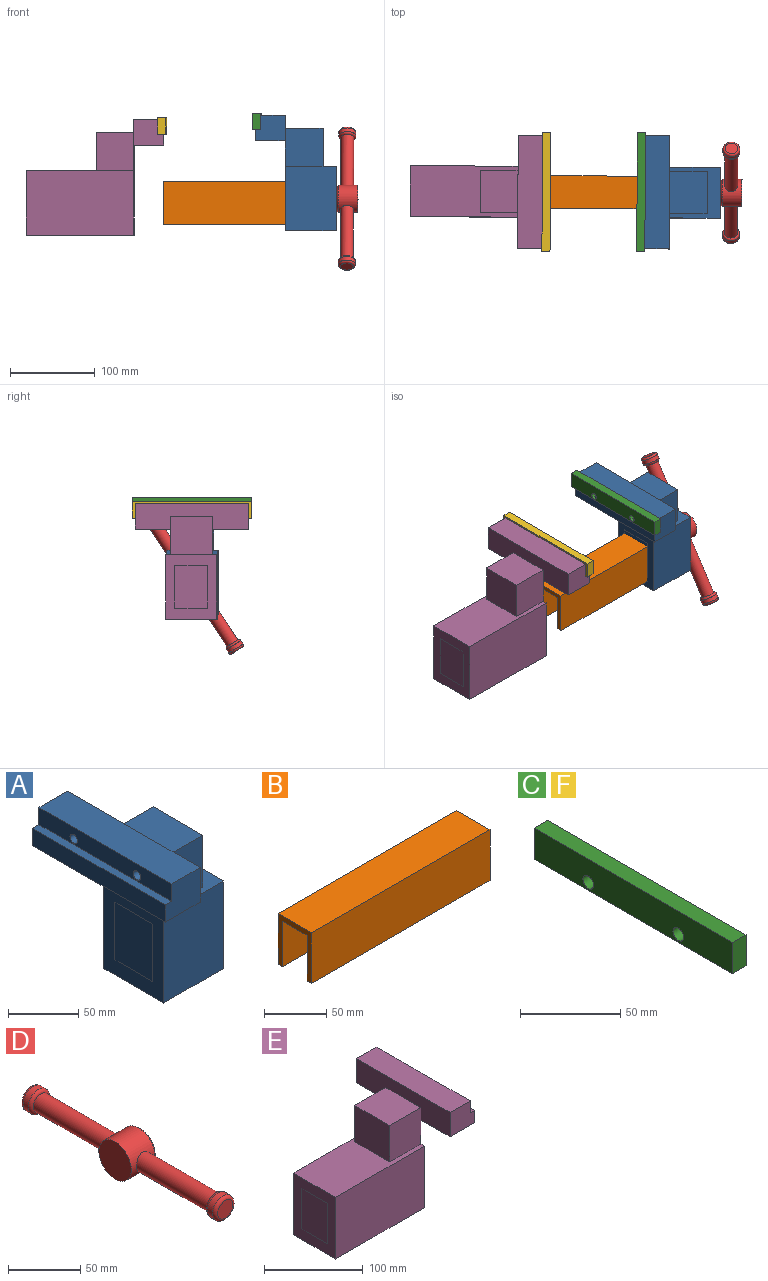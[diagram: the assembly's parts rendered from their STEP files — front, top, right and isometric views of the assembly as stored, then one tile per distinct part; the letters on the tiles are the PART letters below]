
ASSEMBLY  parts=6 mates=5
PART A: 28 faces, bbox 95x133.4x136.2 mm
  f0: plane 35x30mm, normal (0,1,0), area 954.8mm2, adj f11,f12,f13,f14,f16,f17
  f1: plane 106.2x60mm, normal (-1,0,0), area 6072mm2, adj f2,f4,f5,f6,f7,f9,f11
  f2: plane 60x60mm, normal (0,0,1), area 1377.5mm2, adj f1,f3,f5,f6,f7,f8,f9
  f3: plane 76.2x60mm, normal (1,0,0), area 4572mm2, adj f2,f4,f5,f6
  f4: plane 60x60mm, normal (0,0,-1), area 3600mm2, adj f1,f3,f5,f6
  f5: plane 76.2x60mm, normal (0,-1,0), area 4572mm2, adj f1,f2,f3,f4
  f6: plane 76.2x60mm, normal (0,1,0), area 4572mm2, adj f1,f2,f3,f4
  f7: plane 45x44.45mm, normal (0,1,0), area 2000.2mm2, adj f1,f2,f8,f10,f12
  f8: plane 50x45mm, normal (1,0,0), area 2250mm2, adj f2,f7,f9,f10
  f9: plane 45x44.45mm, normal (0,-1,0), area 2000.2mm2, adj f1,f2,f8,f10,f12
  f10: plane 50x44.45mm, normal (0,0,1), area 2222.5mm2, adj f7,f8,f9,f12
  f11: plane 133.35x35mm, normal (0,0,-1), area 4667.2mm2, adj f0,f1,f12,f14,f15
  f12: plane 133.35x30mm, normal (1,0,0), area 3250.5mm2, adj f0,f7,f9,f10,f11,f13,f15
  f13: plane 133.35x28.65mm, normal (0,0,1), area 3820.5mm2, adj f0,f12,f15,f17
  f14: plane 133.35x15mm, normal (-1,0,0), area 2000.2mm2, adj f0,f11,f15,f16
  f15: plane 35x30mm, normal (0,-1,0), area 954.8mm2, adj f11,f12,f13,f14,f16,f17
  f16: plane 133.35x6.35mm, normal (0,0,1), area 846.8mm2, adj f0,f14,f15,f17
  f17: plane 133.35x15mm, normal (-1,0,0), area 1911.9mm2, adj f0,f13,f15,f16,f19,f21
  f18: cone r=0mm half-angle=59deg, axis (-1,0,0), area 51.5mm2, adj f19
  f19: cylinder r=3.75mm len=10mm, axis (-1,0,0), area 235.6mm2, adj f17,f18
  f20: cone r=0mm half-angle=59deg, axis (-1,0,0), area 51.5mm2, adj f21
  f21: cylinder r=3.75mm len=10mm, axis (-1,0,0), area 235.6mm2, adj f17,f20
  f22: plane 50x38.11mm, normal (-1,0,0), area 1905.3mm2, adj f23,f24,f25,f26
  f23: plane 59.8x38.11mm, normal (0,0,1), area 2278.7mm2, adj f22,f25,f26,f27
  f24: plane 59.8x38.11mm, normal (0,0,-1), area 2278.7mm2, adj f22,f25,f26,f27
  f25: plane 59.8x50mm, normal (0,-1,0), area 2990mm2, adj f22,f23,f24,f27
  f26: plane 59.8x50mm, normal (0,1,0), area 2990mm2, adj f22,f23,f24,f27
  f27: plane 50x38.11mm, normal (1,0,0), area 1905.3mm2, adj f23,f24,f25,f26
PART B: 10 faces, bbox 203.4x38.1x50 mm
  f0: plane 203.36x5mm, normal (0,0,-1), area 1016.8mm2, adj f1,f3,f6,f9
  f1: plane 50x38.1mm, normal (1,0,0), area 640.5mm2, adj f0,f2,f4,f5,f6,f7,f8,f9
  f2: plane 203.36x5mm, normal (0,0,-1), area 1016.8mm2, adj f1,f3,f4,f7
  f3: plane 50x38.1mm, normal (-1,0,0), area 640.5mm2, adj f0,f2,f4,f5,f6,f7,f8,f9
  f4: plane 203.36x45mm, normal (0,1,0), area 9151.2mm2, adj f1,f2,f3,f5
  f5: plane 203.36x28.1mm, normal (0,0,-1), area 5714.4mm2, adj f1,f3,f4,f6
  f6: plane 203.36x45mm, normal (0,-1,0), area 9151.2mm2, adj f0,f1,f3,f5
  f7: plane 203.36x50mm, normal (0,-1,0), area 10168mm2, adj f1,f2,f3,f8
  f8: plane 203.36x38.1mm, normal (0,0,1), area 7748mm2, adj f1,f3,f7,f9
  f9: plane 203.36x50mm, normal (0,1,0), area 10168mm2, adj f0,f1,f3,f8
PART C: 8 faces, bbox 9.5x140x19.1 mm
  f0: plane 140x9.53mm, normal (0,0,1), area 1333.5mm2, adj f1,f3,f4,f6
  f1: plane 140x19.05mm, normal (-1,0,0), area 2578.6mm2, adj f0,f2,f4,f5,f6,f7
  f2: plane 140x9.53mm, normal (0,0,-1), area 1333.5mm2, adj f1,f3,f4,f6
  f3: plane 140x19.05mm, normal (1,0,0), area 2578.6mm2, adj f0,f2,f4,f5,f6,f7
  f4: plane 19.05x9.53mm, normal (0,-1,0), area 181.5mm2, adj f0,f1,f2,f3
  f5: cylinder r=3.75mm len=9.53mm, axis (1,0,0), area 224.4mm2, adj f1,f3
  f6: plane 19.05x9.53mm, normal (0,1,0), area 181.5mm2, adj f0,f1,f2,f3
  f7: cylinder r=3.75mm len=9.53mm, axis (1,0,0), area 224.4mm2, adj f1,f3
PART D: 14 faces, bbox 25.4x191x31.8 mm
  f0: cylinder r=15.88mm len=31.75mm, axis (-1,0,0), area 1968.9mm2, adj f2,f3,f4,f9
  f1: plane 27.75x27.75mm, normal (1,0,0), area 604.8mm2, adj f3
  f2: plane 31.75x31.75mm, normal (-1,0,0), area 791.7mm2, adj f0
  f3: cone r=13.88mm half-angle=45deg, axis (-1,0,0), area 264.4mm2, adj f0,f1
  f4: cylinder r=7.5mm len=71.51mm, axis (0,1,0), area 3324.6mm2, adj f0,f7
  f5: cylinder r=10mm len=20mm, axis (0,1,0), area 314.2mm2, adj f7,f8
  f6: plane 15x15mm, normal (0,-1,0), area 176.7mm2, adj f8
  f7: torus R=7.5mm, axis (0,-1,0), area 224.3mm2, adj f4,f5
  f8: torus R=7.5mm, axis (0,-1,0), area 224.3mm2, adj f5,f6
  f9: cylinder r=7.5mm len=71.51mm, axis (0,-1,0), area 3324.6mm2, adj f0,f12
  f10: cylinder r=10mm len=20mm, axis (0,-1,0), area 314.2mm2, adj f12,f13
  f11: plane 15x15mm, normal (0,1,0), area 176.7mm2, adj f13
  f12: torus R=7.5mm, axis (0,1,0), area 224.3mm2, adj f9,f10
  f13: torus R=7.5mm, axis (0,1,0), area 224.3mm2, adj f10,f11
PART E: 27 faces, bbox 162x133.4x136.2 mm
  f0: plane 133.35x15mm, normal (1,0,0), area 2000.2mm2, adj f1,f2,f19,f21
  f1: plane 35x30mm, normal (0,-1,0), area 954.8mm2, adj f0,f17,f18,f19,f20,f21
  f2: plane 35x30mm, normal (0,1,0), area 954.8mm2, adj f0,f17,f18,f19,f20,f21
  f3: plane 127x60mm, normal (0,0,1), area 5397.5mm2, adj f5,f6,f8,f12,f13,f14,f15
  f4: plane 126.9x50mm, normal (0,1,0), area 6345mm2, adj f5,f9,f10,f26
  f5: plane 106.2x60mm, normal (1,0,0), area 4166.7mm2, adj f3,f4,f7,f8,f9,f10,f11,f12
  f6: plane 76.2x60mm, normal (-1,0,0), area 4572mm2, adj f3,f7,f8,f12
  f7: plane 127x60mm, normal (0,0,-1), area 7620mm2, adj f5,f6,f8,f12
  f8: plane 127x76.2mm, normal (0,-1,0), area 9677.4mm2, adj f3,f5,f6,f7
  f9: plane 126.9x38.11mm, normal (0,0,-1), area 4835.5mm2, adj f4,f5,f11,f26
  f10: plane 126.9x38.11mm, normal (0,0,1), area 4835.5mm2, adj f4,f5,f11,f26
  f11: plane 126.9x50mm, normal (0,-1,0), area 6345mm2, adj f5,f9,f10,f26
  f12: plane 127x76.2mm, normal (0,1,0), area 9677.4mm2, adj f3,f5,f6,f7
  f13: plane 45x44.45mm, normal (0,-1,0), area 2000.2mm2, adj f3,f5,f15,f16,f18
  f14: plane 45x44.45mm, normal (0,1,0), area 2000.2mm2, adj f3,f5,f15,f16,f18
  f15: plane 50x45mm, normal (-1,0,0), area 2250mm2, adj f3,f13,f14,f16
  f16: plane 50x44.45mm, normal (0,0,1), area 2222.5mm2, adj f13,f14,f15,f18
  f17: plane 133.35x28.65mm, normal (0,0,1), area 3820.5mm2, adj f1,f2,f18,f20
  f18: plane 133.35x30mm, normal (-1,0,0), area 3250.5mm2, adj f1,f2,f13,f14,f16,f17,f19
  f19: plane 133.35x35mm, normal (0,0,-1), area 4667.2mm2, adj f0,f1,f2,f5,f18
  f20: plane 133.35x15mm, normal (1,0,0), area 1911.9mm2, adj f1,f2,f17,f21,f23,f25
  f21: plane 133.35x6.35mm, normal (0,0,1), area 846.8mm2, adj f0,f1,f2,f20
  f22: cone r=0mm half-angle=59deg, axis (1,0,0), area 51.5mm2, adj f23
  f23: cylinder r=3.75mm len=10mm, axis (1,0,0), area 235.6mm2, adj f20,f22
  f24: cone r=0mm half-angle=59deg, axis (1,0,0), area 51.5mm2, adj f25
  f25: cylinder r=3.75mm len=10mm, axis (1,0,0), area 235.6mm2, adj f20,f24
  f26: plane 50x38.11mm, normal (1,0,0), area 1905.3mm2, adj f4,f9,f10,f11
PART F: same geometry as C
PLACE A rot(axis=(0,0,-1),0.3deg) t=(84.6,-35.63,24.33)mm
PLACE B rot(axis=(0,0,-1),0.3deg) t=(144.6,-35.95,19.39)mm
PLACE C rot(axis=(0,0,-1),0.3deg) t=(51.19,-35.46,114.89)mm
PLACE D rot(axis=(0,0.88,0.48),179.9deg) t=(230,-36.4,24.33)mm
PLACE E rot(axis=(0,0,-1),0.3deg) t=(-93.98,-34.69,19.39)mm fixed
PLACE F rot(axis=(0,0,-1),0.3deg) t=(-60.56,-34.87,109.95)mm
MATE revolute D.f0 <-> A.f3  axis (-1,0.01,0) through (144.6,-35.95,24.33)mm
MATE fastened E.f20 <-> F.f1  axis (1,-0.01,0) through (-65.33,-34.85,110.11)mm
MATE slider B.f3 <-> E.f26  axis (-1,0.01,0) through (-58.65,-15.83,44.39)mm
MATE fastened A.f17 <-> C.f3  axis (-1,0.01,0) through (55.96,-35.48,115.04)mm
MATE fastened B.f1 <-> A.f3  axis (1,-0.01,0) through (144.6,-35.95,24.33)mm
